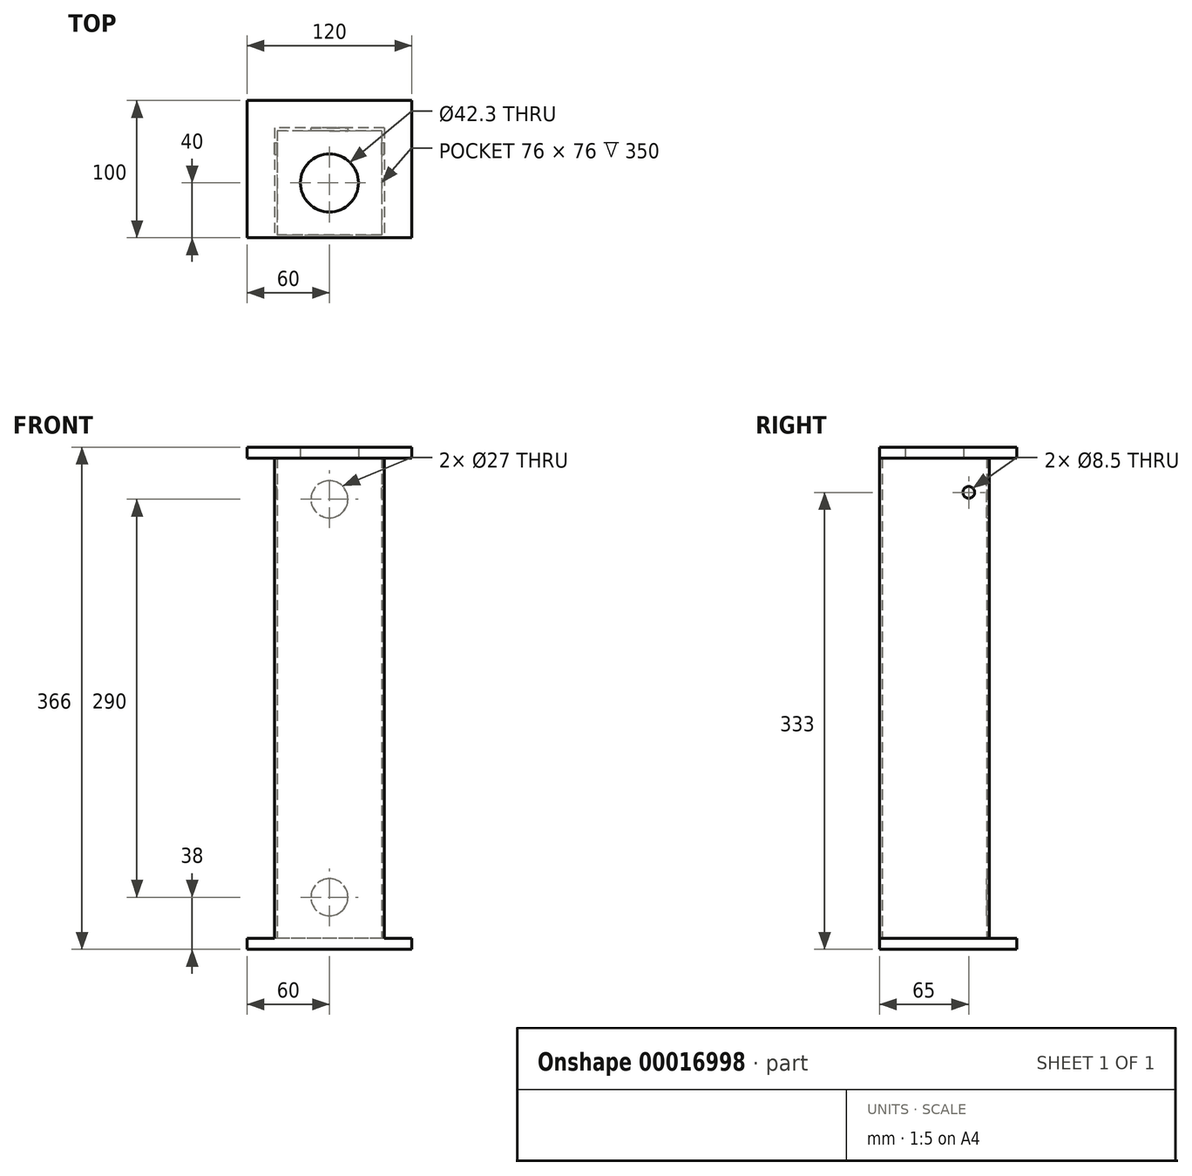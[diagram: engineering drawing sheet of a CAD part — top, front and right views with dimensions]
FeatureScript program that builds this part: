
annotation { "Feature Type Name" : "Feature", "Feature Type Description" : "" }
export const myFeature = defineFeature(function(context is Context, id is Id, definition is map)
    precondition{}
    {
        {
            var Q0;
            Q0=qCreatedBy(makeId("Top.planeOp"),FACE);
            var sketch = newSketch(context, id + "F0", { "sketchPlane" : qUnion([Q0])});
            skLineSegment(sketch, "E0.rect.bottom", {"start": v(60, 60) * mm, "end": v(-60, 60) * mm});
            skLineSegment(sketch, "E0.rect.left", {"start": v(60, 60) * mm, "end": v(60, -40) * mm});
            skLineSegment(sketch, "E0.rect.right", {"start": v(-60, 60) * mm, "end": v(-60, -40) * mm});
            skPoint(sketch, "E0.rect.middle", {"position": v(0, 0) * mm});
            skLineSegment(sketch, "E1.0", {"start": v(60, -40) * mm, "end": v(-60, -40) * mm});
            skSolve(sketch);
        }
        {
            var Q0;
            Q0 = qSketchRegion(id + "F0", true);
            extrude(context, id + "F1", {"entities" : qUnion([Q0]), "oppositeDirection" : true, "depth" : 8 * mm});
        }
        {
            var Q0;
            Q0=makeQuery(id+"F0.imprint","IMPRINT",FACE,{"disambiguationData":[TD([[makeQuery(id+"F0.imprint","IMPRINT",EDGE,{"derivedFrom":sQuery(id+"F0.wireOp",EDGE,"E0.rect.bottom")}),1.0]])]});
            var sketch = newSketch(context, id + "F2", { "sketchPlane" : qUnion([Q0])});
            skLineSegment(sketch, "E2.rect.bottom", {"start": v(40, 40) * mm, "end": v(-40, 40) * mm});
            skLineSegment(sketch, "E2.rect.top", {"start": v(40, -40) * mm, "end": v(-40, -40) * mm});
            skLineSegment(sketch, "E2.rect.left", {"start": v(40, 40) * mm, "end": v(40, -40) * mm});
            skLineSegment(sketch, "E2.rect.right", {"start": v(-40, 40) * mm, "end": v(-40, -40) * mm});
            skPoint(sketch, "E2.rect.middle", {"position": v(0, 0) * mm});
            skLineSegment(sketch, "E3.rect.bottom", {"start": v(38, 38) * mm, "end": v(-38, 38) * mm});
            skLineSegment(sketch, "E3.rect.top", {"start": v(38, -38) * mm, "end": v(-38, -38) * mm});
            skLineSegment(sketch, "E3.rect.left", {"start": v(38, 38) * mm, "end": v(38, -38) * mm});
            skLineSegment(sketch, "E3.rect.right", {"start": v(-38, 38) * mm, "end": v(-38, -38) * mm});
            skSolve(sketch);
        }
        {
            var Q0;
            Q0=makeQuery(id+"F2.imprint","IMPRINT",FACE,{"disambiguationData":[TD([[makeQuery(id+"F2.imprint","IMPRINT",EDGE,{"derivedFrom":sQuery(id+"F2.wireOp",EDGE,"E2.rect.bottom")}),1.0]])]});
            extrude(context, id + "F3", {"entities" : qUnion([Q0]), "operationType" : NewBodyOperationType.ADD, "depth" : 350 * mm});
        }
        {
            var Q0;
            Q0=makeQuery(id+"F3.opExtrude","CAP_FACE",FACE,{"disambiguationData":[OSD([sQuery(id+"F2.wireOp",EDGE,"E2.rect.bottom"),sQuery(id+"F2.wireOp",EDGE,"E2.rect.top"),sQuery(id+"F2.wireOp",EDGE,"E2.rect.left"),sQuery(id+"F2.wireOp",EDGE,"E2.rect.right"),sQuery(id+"F2.wireOp",EDGE,"E3.rect.bottom"),sQuery(id+"F2.wireOp",EDGE,"E3.rect.top"),sQuery(id+"F2.wireOp",EDGE,"E3.rect.left"),sQuery(id+"F2.wireOp",EDGE,"E3.rect.right")])],"isStart":false});
            var sketch = newSketch(context, id + "F4", { "sketchPlane" : qUnion([Q0])});
            skLineSegment(sketch, "E4", {"start": v(-40, 40) * mm, "end": v(40, -40) * mm, "construction": true});
            skLineSegment(sketch, "E5.rect.bottom", {"start": v(60, 60) * mm, "end": v(-60, 60) * mm});
            skLineSegment(sketch, "E5.rect.left", {"start": v(60, 60) * mm, "end": v(60, -40) * mm});
            skLineSegment(sketch, "E5.rect.right", {"start": v(-60, 60) * mm, "end": v(-60, -40) * mm});
            skPoint(sketch, "E5.rect.middle", {"position": v(0, 0) * mm});
            skCircle(sketch, "E6", {"center": v(0, 0) * mm, "radius": 21.15 * mm});
            skLineSegment(sketch, "E7.0", {"start": v(60, -40) * mm, "end": v(-60, -40) * mm});
            skSolve(sketch);
        }
        {
            var Q0;
            Q0 = qSketchRegion(id + "F4", true);
            extrude(context, id + "F5", {"entities" : qUnion([Q0]), "depth" : 8 * mm});
        }
        {
            var Q0;
            Q0=makeQuery(id+"F3.opExtrude","SWEPT_FACE",FACE,{"disambiguationData":[OSD([sQuery(id+"F2.wireOp",EDGE,"E2.rect.bottom")])]});
            var sketch = newSketch(context, id + "F6", { "sketchPlane" : qUnion([Q0])});
            skPoint(sketch, "E8", {"position": v(0, 320) * mm});
            skCircle(sketch, "E9", {"center": v(0, 320) * mm, "radius": 13.5 * mm});
            skPoint(sketch, "E10", {"position": v(0, 30) * mm});
            skCircle(sketch, "E11", {"center": v(0, 30) * mm, "radius": 13.5 * mm});
            skSolve(sketch);
        }
        {
            var Q0;
            Q0=makeQuery(id+"F6.imprint","IMPRINT",FACE,{"disambiguationData":[TD([[makeQuery(id+"F6.imprint","IMPRINT",EDGE,{"derivedFrom":sQuery(id+"F6.wireOp",EDGE,"E11")}),1.0]])]});
            var Q1;
            Q1=makeQuery(id+"F6.imprint","IMPRINT",FACE,{"disambiguationData":[TD([[makeQuery(id+"F6.imprint","IMPRINT",EDGE,{"derivedFrom":sQuery(id+"F6.wireOp",EDGE,"E9")}),1.0]])]});
            extrude(context, id + "F7", {"entities" : qUnion([Q0, Q1]), "operationType" : NewBodyOperationType.REMOVE, "oppositeDirection" : true, "depth" : 25 * mm});
        }
        {
            var Q0;
            Q0=makeQuery(id+"F3.opExtrude","SWEPT_FACE",FACE,{"disambiguationData":[OSD([sQuery(id+"F2.wireOp",EDGE,"E2.rect.left")])]});
            var sketch = newSketch(context, id + "F8", { "sketchPlane" : qUnion([Q0])});
            skPoint(sketch, "E12", {"position": v(25, 325) * mm});
            skSolve(sketch);
        }
        {
            var Q0;
            Q0=sQuery(id+"F8.wireOp",VERTEX,"E12");
            var Q1;
            Q1=makeQuery(id+"F1.opExtrude","SWEPT_BODY",BODY,{"disambiguationData":[OSD([sQuery(id+"F0.wireOp",EDGE,"E0.rect.bottom"),sQuery(id+"F0.wireOp",EDGE,"E0.rect.left"),sQuery(id+"F0.wireOp",EDGE,"E0.rect.right"),sQuery(id+"F0.wireOp",EDGE,"E1.0")])]});
            hole(context, id + "F9", {"style" : HoleStyle.SIMPLE, "holeDiameter" : 8.5 * mm, "endStyle" : HoleEndStyle.THROUGH, "locations" : qUnion([Q0]), "scope" : qUnion([Q1])});
        }
    });
